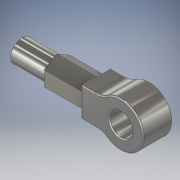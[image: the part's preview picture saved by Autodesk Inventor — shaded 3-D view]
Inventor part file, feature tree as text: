
AUTODESK INVENTOR PART (.ipt)
format: ipt  version: 2018 (Build 220112000, 112)  size: 189,440 bytes
history: native  units: in
note: dims shown in document units (in); Inventor stores cm internally (conversion verified against a paired STEP export)
features: extrude x3, fillet x3, sketch x3, chamfer x1
ambient origin geometry x8: Origin, YZ Plane, XZ Plane, XY Plane, X Axis, Y Axis, Z Axis, Center Point
bodies: Solid1 (feature_tree)
feature tree (10):
  extrude  "Extrusion1"  Depth=1.378in TaperAngle=0.0deg
  extrude  "Extrusion2"  Depth=0.7874in
  extrude  "Extrusion3"  Depth=0.0394in TaperAngle=45.0deg
  fillet  "Fillet1"  Radius=0.0394in
  fillet  "Fillet2"  [1 undecoded]
  chamfer  "Chamfer1"  [1 undecoded]
  fillet  "Fillet3"  [1 undecoded]
  sketch  "Sketch1"  dims[d6=1.0236in d7=0.0in d8=1.378in d9=0.0in]
  sketch  "Sketch2"  dims[d10=1.1811in d11=0.0in d12=0.7874in]
  sketch  "Sketch3"  dims[d13=0.7874in d14=0.0394in d15=0.0787in d16=45.0deg d17=0.0394in]
note: 3 required parameter values undecoded (feature->parameter linkage not recoverable at this tier; creation-order binding heuristic only, values carry confidence <= 0.55)
